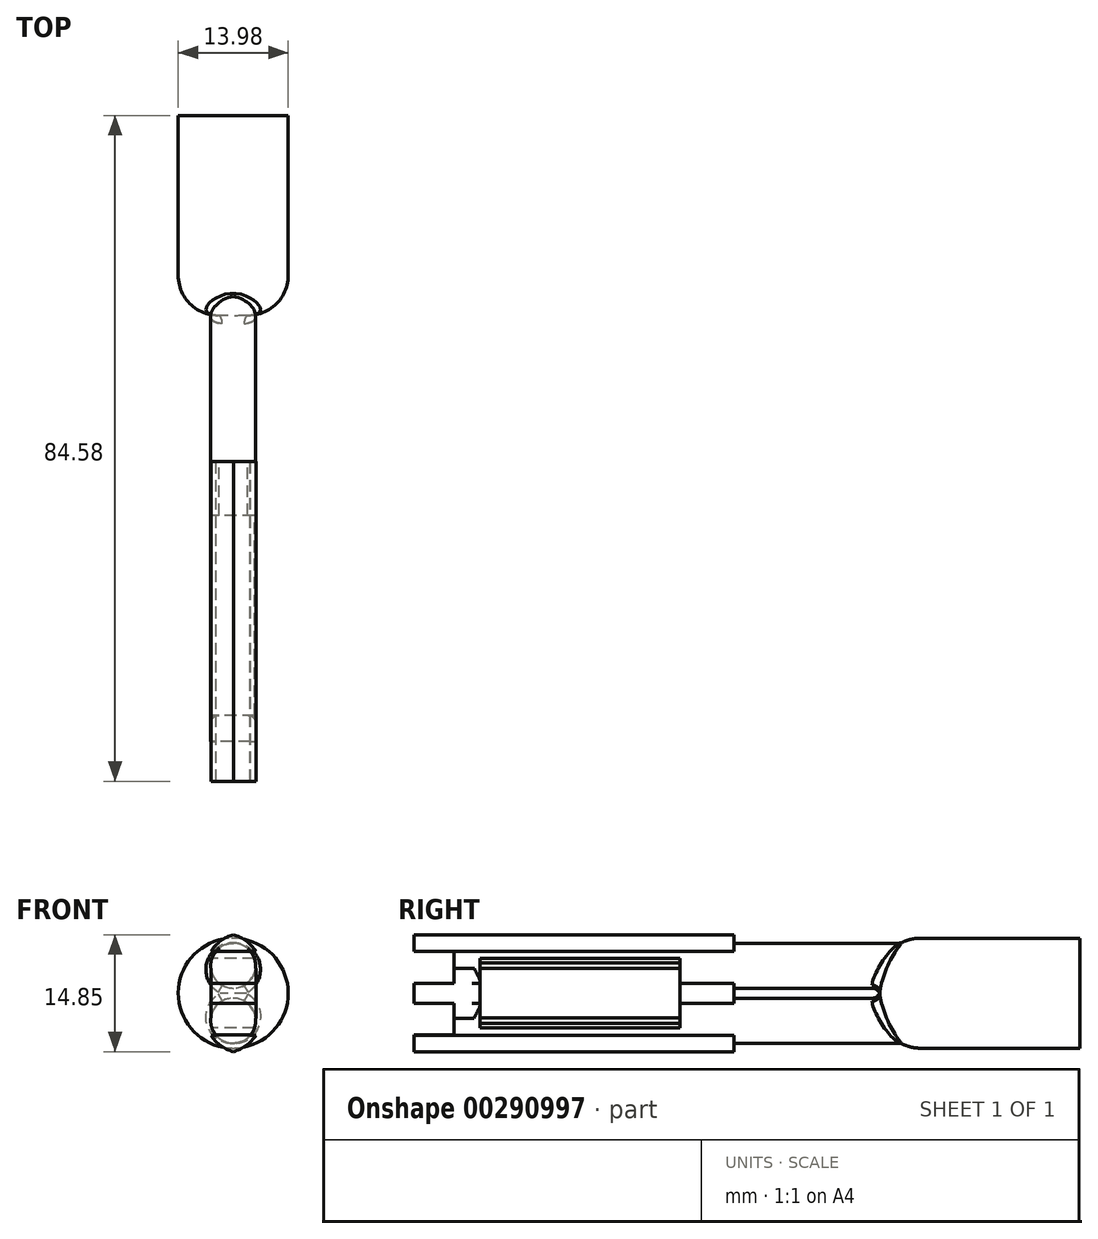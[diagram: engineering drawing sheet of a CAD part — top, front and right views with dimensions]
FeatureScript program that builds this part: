
annotation { "Feature Type Name" : "Feature", "Feature Type Description" : "" }
export const myFeature = defineFeature(function(context is Context, id is Id, definition is map)
    precondition{}
    {
        {
            var Q0;
            Q0=qCreatedBy(makeId("Front.planeOp"),FACE);
            var sketch = newSketch(context, id + "F0", { "sketchPlane" : qUnion([Q0])});
            skCircle(sketch, "E0", {"center": v(0, 0) * mm, "radius": 6.99 * mm});
            skSolve(sketch);
        }
        {
            var Q0;
            Q0=qCreatedBy(makeId("Right.planeOp"),FACE);
            var sketch = newSketch(context, id + "F1", { "sketchPlane" : qUnion([Q0])});
            skLineSegment(sketch, "E1", {"start": v(0, 0) * mm, "end": v(-25.4, 0) * mm});
            skSolve(sketch);
        }
        {
            var Q0;
            Q0 = qSketchRegion(id + "F0", true);
            var Q1;
            Q1 = qConstructionFilter(qBodyType(qCreatedBy(id + "F1" ,EDGE), BodyType.WIRE), ConstructionObject.NO);
            sweep(context, id + "F2", {"profiles" : qUnion([Q0]), "path" : qUnion([Q1])});
        }
        {
            var Q0;
            Q0=makeQuery(id+"F2.opSweep","CAP_FACE",FACE,{"disambiguationData":[OSD([sQuery(id+"F0.wireOp",EDGE,"E0"),sQuery(id+"F1.wireOp",VERTEX,"E1.end")])],"isStart":false});
            var sketch = newSketch(context, id + "F3", { "sketchPlane" : qUnion([Q0])});
            skLineSegment(sketch, "E2", {"start": v(0, 0) * mm, "end": v(0, 6.99) * mm});
            skLineSegment(sketch, "E3", {"start": v(0, -6.99) * mm, "end": v(0, 0) * mm});
            skCircle(sketch, "E4", {"center": v(0, 3.5) * mm, "radius": 2.86 * mm});
            skCircle(sketch, "E5", {"center": v(0, -3.5) * mm, "radius": 2.86 * mm});
            skSolve(sketch);
        }
        {
            var Q0;
            Q0=qCreatedBy(makeId("Right.planeOp"),FACE);
            var sketch = newSketch(context, id + "F4", { "sketchPlane" : qUnion([Q0])});
            skSolve(sketch);
        }
        {
            var Q0;
            Q0 = qSketchRegion(id + "F4", true);
            var Q1;
            {var subQ0=sQuery(id+"F3.wireOp",EDGE,"E4");var subQ1=sQuery(id+"F3.wireOp",EDGE,"E2");var subQ2=makeQuery(id+"F3.imprint","INTERSECT",VERTEX,{"disambiguationData":[OD(0.0)],"derivedFrom":[subQ1,subQ0]});Q1=makeQuery(id+"F3.imprint","IMPRINT",FACE,{"disambiguationData":[TD([[makeQuery(id+"F3.imprint","IMPRINT",EDGE,{"disambiguationData":[TD([[subQ2,-1.0]])],"derivedFrom":subQ1}),1.0]])]});}
            var Q2;
            {var subQ0=sQuery(id+"F3.wireOp",EDGE,"E4");var subQ1=sQuery(id+"F3.wireOp",EDGE,"E2");var subQ2=makeQuery(id+"F3.imprint","INTERSECT",VERTEX,{"disambiguationData":[OD(0.0)],"derivedFrom":[subQ1,subQ0]});Q2=makeQuery(id+"F3.imprint","IMPRINT",FACE,{"disambiguationData":[TD([[makeQuery(id+"F3.imprint","IMPRINT",EDGE,{"disambiguationData":[TD([[subQ2,-1.0]])],"derivedFrom":subQ1}),-1.0]])]});}
            var Q3;
            {var subQ0=sQuery(id+"F3.wireOp",EDGE,"E5");var subQ1=sQuery(id+"F3.wireOp",EDGE,"E3");var subQ2=makeQuery(id+"F3.imprint","INTERSECT",VERTEX,{"disambiguationData":[OD(0.0)],"derivedFrom":[subQ1,subQ0]});Q3=makeQuery(id+"F3.imprint","IMPRINT",FACE,{"disambiguationData":[TD([[makeQuery(id+"F3.imprint","IMPRINT",EDGE,{"disambiguationData":[TD([[subQ2,-1.0]])],"derivedFrom":subQ1}),1.0]])]});}
            var Q4;
            {var subQ0=sQuery(id+"F3.wireOp",EDGE,"E5");var subQ1=sQuery(id+"F3.wireOp",EDGE,"E3");var subQ2=makeQuery(id+"F3.imprint","INTERSECT",VERTEX,{"disambiguationData":[OD(0.0)],"derivedFrom":[subQ1,subQ0]});Q4=makeQuery(id+"F3.imprint","IMPRINT",FACE,{"disambiguationData":[TD([[makeQuery(id+"F3.imprint","IMPRINT",EDGE,{"disambiguationData":[TD([[subQ2,-1.0]])],"derivedFrom":subQ1}),-1.0]])]});}
            extrude(context, id + "F5", {"entities" : qUnion([Q0, Q1, Q2, Q3, Q4]), "operationType" : NewBodyOperationType.ADD, "depth" : 50.8 * mm});
        }
        {
            var Q0;
            Q0=makeQuery(id+"F5.opExtrude","CAP_FACE",FACE,{"disambiguationData":[OSD([sQuery(id+"F3.wireOp",EDGE,"E4")])],"isStart":false});
            var sketch = newSketch(context, id + "F6", { "sketchPlane" : qUnion([Q0])});
            skLineSegment(sketch, "E6.bottom", {"start": v(-2.84, 3.15) * mm, "end": v(2.88, 3.15) * mm});
            skLineSegment(sketch, "E6.top", {"start": v(-2.84, -3.2) * mm, "end": v(2.88, -3.2) * mm});
            skLineSegment(sketch, "E6.left", {"start": v(-2.84, 3.15) * mm, "end": v(-2.84, -3.2) * mm});
            skLineSegment(sketch, "E6.right", {"start": v(2.88, 3.15) * mm, "end": v(2.88, -3.2) * mm});
            skSolve(sketch);
        }
        {
            var Q0;
            Q0=makeQuery(id+"F5.opExtrude","CAP_FACE",FACE,{"disambiguationData":[OSD([sQuery(id+"F3.wireOp",EDGE,"E5")])],"isStart":false});
            var Q1;
            {var subQ0=sQuery(id+"F6.wireOp",EDGE,"E6.bottom");var subQ1=makeQuery(id+"F5.opExtrude","CAP_EDGE",EDGE,{"disambiguationData":[OSD([sQuery(id+"F3.wireOp",EDGE,"E4")])],"isStart":false});var subQ3=makeQuery(id+"F6.imprint","INTERSECT",VERTEX,{"derivedFrom":[subQ1,subQ0]});Q1=makeQuery(id+"F6.imprint","IMPRINT",FACE,{"disambiguationData":[TD([[makeQuery(id+"F6.imprint","IMPRINT",EDGE,{"disambiguationData":[TD([[subQ3,1.0]])],"derivedFrom":subQ0}),-1.0]])]});}
            var Q2;
            Q2=makeQuery(id+"F6.imprint","IMPRINT",FACE,{"disambiguationData":[TD([[makeQuery(id+"F6.imprint","IMPRINT",EDGE,{"derivedFrom":sQuery(id+"F6.wireOp",EDGE,"E6.top")}),1.0]])]});
            var Q3;
            {var subQ0=sQuery(id+"F6.wireOp",EDGE,"E6.bottom");var subQ1=makeQuery(id+"F5.opExtrude","CAP_EDGE",EDGE,{"disambiguationData":[OSD([sQuery(id+"F3.wireOp",EDGE,"E4")])],"isStart":false});var subQ3=makeQuery(id+"F6.imprint","INTERSECT",VERTEX,{"derivedFrom":[subQ1,subQ0]});Q3=makeQuery(id+"F6.imprint","IMPRINT",FACE,{"disambiguationData":[TD([[makeQuery(id+"F6.imprint","IMPRINT",EDGE,{"disambiguationData":[TD([[subQ3,1.0]])],"derivedFrom":subQ0}),1.0]])]});}
            extrude(context, id + "F7", {"entities" : qUnion([Q0, Q1, Q2, Q3]), "operationType" : NewBodyOperationType.ADD, "depth" : 8.38 * mm});
        }
        {
            var Q0;
            Q0=makeQuery(id+"F7.boolean.opBoolean","MERGE",FACE,{"derivedFrom":[makeQuery(id+"F7.opExtrude","CAP_FACE",FACE,{"disambiguationData":[OSD([sQuery(id+"F3.wireOp",EDGE,"E5")])],"isStart":false}),makeQuery(id+"F7.opExtrude","CAP_FACE",FACE,{"disambiguationData":[OSD([sQuery(id+"F3.wireOp",EDGE,"E4"),sQuery(id+"F6.wireOp",EDGE,"E6.bottom"),sQuery(id+"F6.wireOp",EDGE,"E6.top"),sQuery(id+"F6.wireOp",EDGE,"E6.left"),sQuery(id+"F6.wireOp",EDGE,"E6.right")])],"isStart":false})]});
            var sketch = newSketch(context, id + "F8", { "sketchPlane" : qUnion([Q0])});
            skLineSegment(sketch, "E7", {"start": v(-2.84, 0) * mm, "end": v(-2.84, -1.27) * mm});
            skLineSegment(sketch, "E8", {"start": v(-2.84, -1.27) * mm, "end": v(2.88, -1.27) * mm});
            skLineSegment(sketch, "E9", {"start": v(2.88, -1.27) * mm, "end": v(2.88, -5.3) * mm});
            skLineSegment(sketch, "E10", {"start": v(2.88, -5.3) * mm, "end": v(-2.84, -5.3) * mm});
            skLineSegment(sketch, "E11", {"start": v(-2.84, -1.27) * mm, "end": v(-2.84, -5.3) * mm});
            skLineSegment(sketch, "E12", {"start": v(-2.84, 0) * mm, "end": v(-2.84, 1.27) * mm});
            skLineSegment(sketch, "E13", {"start": v(-2.84, 1.27) * mm, "end": v(2.88, 1.27) * mm});
            skLineSegment(sketch, "E14", {"start": v(2.88, 1.27) * mm, "end": v(2.88, 5.3) * mm});
            skLineSegment(sketch, "E15", {"start": v(2.88, 5.3) * mm, "end": v(-2.84, 5.3) * mm});
            skLineSegment(sketch, "E16", {"start": v(-2.84, 1.27) * mm, "end": v(-2.84, 5.3) * mm});
            skSolve(sketch);
        }
        {
            var Q0;
            Q0 = qSketchRegion(id + "F8", true);
            extrude(context, id + "F9", {"entities" : qUnion([Q0]), "operationType" : NewBodyOperationType.REMOVE, "oppositeDirection" : true, "depth" : 5.08 * mm});
        }
        {
            var Q0;
            Q0=makeQuery(id+"F7.opExtrude","SWEPT_FACE",FACE,{"disambiguationData":[OSD([sQuery(id+"F6.wireOp",EDGE,"E6.left")])]});
            var sketch = newSketch(context, id + "F10", { "sketchPlane" : qUnion([Q0])});
            skLineSegment(sketch, "E17", {"start": v(76.2, 0) * mm, "end": v(76.2, 3.15) * mm});
            skLineSegment(sketch, "E18", {"start": v(50.8, 3.15) * mm, "end": v(50.8, -3.15) * mm});
            skLineSegment(sketch, "E19", {"start": v(76.2, -3.15) * mm, "end": v(76.2, 0) * mm});
            skLineSegment(sketch, "E20.0", {"start": v(76.2, 4.42) * mm, "end": v(50.8, 4.42) * mm});
            skLineSegment(sketch, "E21.0", {"start": v(50.8, -4.42) * mm, "end": v(76.2, -4.42) * mm});
            skLineSegment(sketch, "E22", {"start": v(50.8, -4.42) * mm, "end": v(50.8, -3.15) * mm});
            skLineSegment(sketch, "E23", {"start": v(50.8, 3.15) * mm, "end": v(50.8, 4.42) * mm});
            skLineSegment(sketch, "E24", {"start": v(76.2, 3.15) * mm, "end": v(76.2, 4.42) * mm});
            skLineSegment(sketch, "E25", {"start": v(76.2, -4.42) * mm, "end": v(76.2, -3.15) * mm});
            skSolve(sketch);
        }
        {
            var Q0;
            Q0=makeQuery(id+"F2.opSweep","CAP_EDGE",EDGE,{"disambiguationData":[OSD([sQuery(id+"F0.wireOp",EDGE,"E0"),sQuery(id+"F1.wireOp",VERTEX,"E1.end")])],"isStart":false});
            fillet(context, id + "F11", {"entities" : qUnion([Q0]), "radius" : 5.08 * mm, "tangentPropagation" : true, "allowEdgeOverflow" : false});
        }
        {
            var Q0;
            {var subQ0=sQuery(id+"F3.wireOp",EDGE,"E4");Q0=makeQuery(id+"F11.opFillet","BLEND_EDGE",EDGE,{"blendedFrom":[makeQuery(id+"F2.opSweep","CAP_EDGE",EDGE,{"disambiguationData":[OSD([sQuery(id+"F0.wireOp",EDGE,"E0"),sQuery(id+"F1.wireOp",VERTEX,"E1.end")])],"isStart":false}),makeQuery(id+"F7.boolean.opBoolean","MERGE",FACE,{"derivedFrom":[makeQuery(id+"F5.opExtrude","SWEPT_FACE",FACE,{"disambiguationData":[OSD([subQ0])]}),makeQuery(id+"F7.opExtrude","SWEPT_FACE",FACE,{"disambiguationData":[OSD([subQ0])]})]})],"blendedInto":[makeQuery(id+"F7.boolean.opBoolean","MERGE",FACE,{"derivedFrom":[makeQuery(id+"F5.opExtrude","SWEPT_FACE",FACE,{"disambiguationData":[OSD([subQ0])]}),makeQuery(id+"F7.opExtrude","SWEPT_FACE",FACE,{"disambiguationData":[OSD([subQ0])]})]})]});}
            var Q1;
            {var subQ0=sQuery(id+"F3.wireOp",EDGE,"E5");Q1=makeQuery(id+"F11.opFillet","BLEND_EDGE",EDGE,{"blendedFrom":[makeQuery(id+"F2.opSweep","CAP_EDGE",EDGE,{"disambiguationData":[OSD([sQuery(id+"F0.wireOp",EDGE,"E0"),sQuery(id+"F1.wireOp",VERTEX,"E1.end")])],"isStart":false}),makeQuery(id+"F7.boolean.opBoolean","MERGE",FACE,{"derivedFrom":[makeQuery(id+"F5.opExtrude","SWEPT_FACE",FACE,{"disambiguationData":[OSD([subQ0])]}),makeQuery(id+"F7.opExtrude","SWEPT_FACE",FACE,{"disambiguationData":[OSD([subQ0])]})]})],"blendedInto":[makeQuery(id+"F7.boolean.opBoolean","MERGE",FACE,{"derivedFrom":[makeQuery(id+"F5.opExtrude","SWEPT_FACE",FACE,{"disambiguationData":[OSD([subQ0])]}),makeQuery(id+"F7.opExtrude","SWEPT_FACE",FACE,{"disambiguationData":[OSD([subQ0])]})]})]});}
            var Q2;
            {var subQ0=sQuery(id+"F3.wireOp",EDGE,"E5");Q2=makeQuery(id+"F18.boolean.opBoolean","INTERSECT",EDGE,{"derivedFrom":[makeQuery(id+"F7.boolean.opBoolean","MERGE",FACE,{"derivedFrom":[makeQuery(id+"F5.opExtrude","SWEPT_FACE",FACE,{"disambiguationData":[OSD([subQ0])]}),makeQuery(id+"F7.opExtrude","SWEPT_FACE",FACE,{"disambiguationData":[OSD([subQ0])]})]}),makeQuery(id+"F18.opExtrude","SWEPT_FACE",FACE,{"disambiguationData":[OSD([sQuery(id+"F10.wireOp",EDGE,"E18")])]})]});}
            var Q3;
            {var subQ0=sQuery(id+"F3.wireOp",EDGE,"E4");Q3=makeQuery(id+"F18.boolean.opBoolean","INTERSECT",EDGE,{"derivedFrom":[makeQuery(id+"F7.boolean.opBoolean","MERGE",FACE,{"derivedFrom":[makeQuery(id+"F5.opExtrude","SWEPT_FACE",FACE,{"disambiguationData":[OSD([subQ0])]}),makeQuery(id+"F7.opExtrude","SWEPT_FACE",FACE,{"disambiguationData":[OSD([subQ0])]})]}),makeQuery(id+"F18.opExtrude","SWEPT_FACE",FACE,{"disambiguationData":[OSD([sQuery(id+"F10.wireOp",EDGE,"E18")])]})]});}
            var Q4;
            Q4=makeQuery(id+"F7.opExtrude","CAP_EDGE",EDGE,{"disambiguationData":[OSD([sQuery(id+"F6.wireOp",EDGE,"E6.left")])],"isStart":true});
            var Q5;
            Q5=makeQuery(id+"F7.opExtrude","CAP_EDGE",EDGE,{"disambiguationData":[OSD([sQuery(id+"F6.wireOp",EDGE,"E6.right")])],"isStart":true});
            fillet(context, id + "F12", {"entities" : qUnion([Q0, Q1, Q2, Q3, Q4, Q5]), "radius" : 1.02 * mm, "tangentPropagation" : true, "allowEdgeOverflow" : false});
        }
        {
            var Q0;
            Q0=qCreatedBy(makeId("Right.planeOp"),FACE);
            var sketch = newSketch(context, id + "F13", { "sketchPlane" : qUnion([Q0])});
            skPoint(sketch, "E26.0", {"position": v(-84.58, 3.83) * mm});
            skLineSegment(sketch, "E27.bottom", {"start": v(-84.67, 3.09) * mm, "end": v(-79.5, 3.09) * mm});
            skLineSegment(sketch, "E27.top", {"start": v(-84.67, 3.84) * mm, "end": v(-79.5, 3.84) * mm});
            skLineSegment(sketch, "E27.left", {"start": v(-84.67, 3.09) * mm, "end": v(-84.67, 3.84) * mm});
            skLineSegment(sketch, "E27.right", {"start": v(-79.5, 3.09) * mm, "end": v(-79.5, 3.84) * mm});
            skLineSegment(sketch, "E28.bottom", {"start": v(-84.65, -4.05) * mm, "end": v(-79.5, -4.05) * mm});
            skLineSegment(sketch, "E28.top", {"start": v(-84.65, -2.95) * mm, "end": v(-79.5, -2.95) * mm});
            skLineSegment(sketch, "E28.left", {"start": v(-84.65, -4.05) * mm, "end": v(-84.65, -2.95) * mm});
            skLineSegment(sketch, "E28.right", {"start": v(-79.5, -4.05) * mm, "end": v(-79.5, -2.95) * mm});
            skSolve(sketch);
        }
        {
            var Q0;
            Q0 = qSketchRegion(id + "F13", true);
            extrude(context, id + "F14", {"entities" : qUnion([Q0]), "operationType" : NewBodyOperationType.REMOVE, "oppositeDirection" : true, "depth" : 25.4 * mm});
        }
        {
            var Q0;
            {var subQ0=sQuery(id+"F6.wireOp",EDGE,"E6.left");var subQ1=sQuery(id+"F6.wireOp",EDGE,"E6.right");Q0=makeQuery(id+"F9.boolean.opBoolean","SPLIT",FACE,{"disambiguationData":[TD([makeQuery(id+"F7.opExtrude","SWEPT_FACE",FACE,{"disambiguationData":[OSD([subQ0])]})])],"derivedFrom":makeQuery(id+"F7.boolean.opBoolean","MERGE",FACE,{"derivedFrom":[makeQuery(id+"F7.opExtrude","CAP_FACE",FACE,{"disambiguationData":[OSD([sQuery(id+"F3.wireOp",EDGE,"E5")])],"isStart":false}),makeQuery(id+"F7.opExtrude","CAP_FACE",FACE,{"disambiguationData":[OSD([sQuery(id+"F3.wireOp",EDGE,"E4"),sQuery(id+"F6.wireOp",EDGE,"E6.bottom"),sQuery(id+"F6.wireOp",EDGE,"E6.top"),subQ0,subQ1])],"isStart":false})]})});}
            var sketch = newSketch(context, id + "F15", { "sketchPlane" : qUnion([Q0])});
            skLineSegment(sketch, "E29", {"start": v(-2.84, 0) * mm, "end": v(-2.84, 7.62) * mm});
            skLineSegment(sketch, "E30", {"start": v(-2.84, 7.62) * mm, "end": v(2.88, 7.62) * mm});
            skLineSegment(sketch, "E31", {"start": v(2.88, 7.62) * mm, "end": v(2.88, 0) * mm});
            skLineSegment(sketch, "E32", {"start": v(-2.84, 5.32) * mm, "end": v(2.88, 5.32) * mm});
            skLineSegment(sketch, "E33", {"start": v(-2.84, 0) * mm, "end": v(-2.84, -7.62) * mm});
            skLineSegment(sketch, "E34", {"start": v(-2.84, -7.62) * mm, "end": v(2.88, -7.62) * mm});
            skLineSegment(sketch, "E35", {"start": v(2.88, -7.62) * mm, "end": v(2.88, 0) * mm});
            skLineSegment(sketch, "E36", {"start": v(-2.84, -5.36) * mm, "end": v(2.88, -5.36) * mm});
            skSolve(sketch);
        }
        {
            var Q0;
            {var subQ0=sQuery(id+"F15.wireOp",EDGE,"E34");Q0=makeQuery(id+"F15.imprint","IMPRINT",FACE,{"disambiguationData":[TD([[makeQuery(id+"F15.imprint","IMPRINT",EDGE,{"derivedFrom":subQ0}),1.0]])]});}
            var Q1;
            {var subQ0=makeQuery(id+"F9.boolean.opBoolean","COPY",EDGE,{"derivedFrom":makeQuery(id+"F9.opExtrude","CAP_EDGE",EDGE,{"disambiguationData":[OSD([sQuery(id+"F8.wireOp",EDGE,"E8")])],"isStart":true})});Q1=makeQuery(id+"F15.imprint","IMPRINT",FACE,{"disambiguationData":[TD([[makeQuery(id+"F15.imprint","IMPRINT",EDGE,{"derivedFrom":subQ0}),1.0]])]});}
            var Q2;
            {var subQ0=sQuery(id+"F15.wireOp",EDGE,"E30");Q2=makeQuery(id+"F15.imprint","IMPRINT",FACE,{"disambiguationData":[TD([[makeQuery(id+"F15.imprint","IMPRINT",EDGE,{"derivedFrom":subQ0}),-1.0]])]});}
            extrude(context, id + "F16", {"entities" : qUnion([Q0, Q1, Q2]), "operationType" : NewBodyOperationType.ADD, "oppositeDirection" : true, "depth" : 40.64 * mm});
        }
        {
            var Q0;
            Q0=makeQuery(id+"F16.opExtrude","SWEPT_EDGE",EDGE,{"disambiguationData":[OSD([sQuery(id+"F15.wireOp",EDGE,"E30"),sQuery(id+"F15.wireOp",EDGE,"E31")])]});
            var Q1;
            Q1=makeQuery(id+"F16.opExtrude","SWEPT_EDGE",EDGE,{"disambiguationData":[OSD([sQuery(id+"F15.wireOp",EDGE,"E29"),sQuery(id+"F15.wireOp",EDGE,"E30")])]});
            var Q2;
            Q2=makeQuery(id+"F16.opExtrude","SWEPT_EDGE",EDGE,{"disambiguationData":[OSD([sQuery(id+"F15.wireOp",EDGE,"E33"),sQuery(id+"F15.wireOp",EDGE,"E34")])]});
            var Q3;
            Q3=makeQuery(id+"F16.opExtrude","SWEPT_EDGE",EDGE,{"disambiguationData":[OSD([sQuery(id+"F15.wireOp",EDGE,"E34"),sQuery(id+"F15.wireOp",EDGE,"E35")])]});
            fillet(context, id + "F17", {"entities" : qUnion([Q0, Q1, Q2, Q3]), "radius" : 5.08 * mm, "tangentPropagation" : true, "allowEdgeOverflow" : false});
        }
        {
            var Q0;
            Q0=makeQuery(id+"F10.imprint","IMPRINT",FACE,{"disambiguationData":[TD([[makeQuery(id+"F10.imprint","IMPRINT",EDGE,{"derivedFrom":sQuery(id+"F10.wireOp",EDGE,"E17")}),-1.0]])]});
            extrude(context, id + "F18", {"entities" : qUnion([Q0]), "operationType" : NewBodyOperationType.REMOVE, "oppositeDirection" : true, "depth" : 25.4 * mm});
        }
    });
